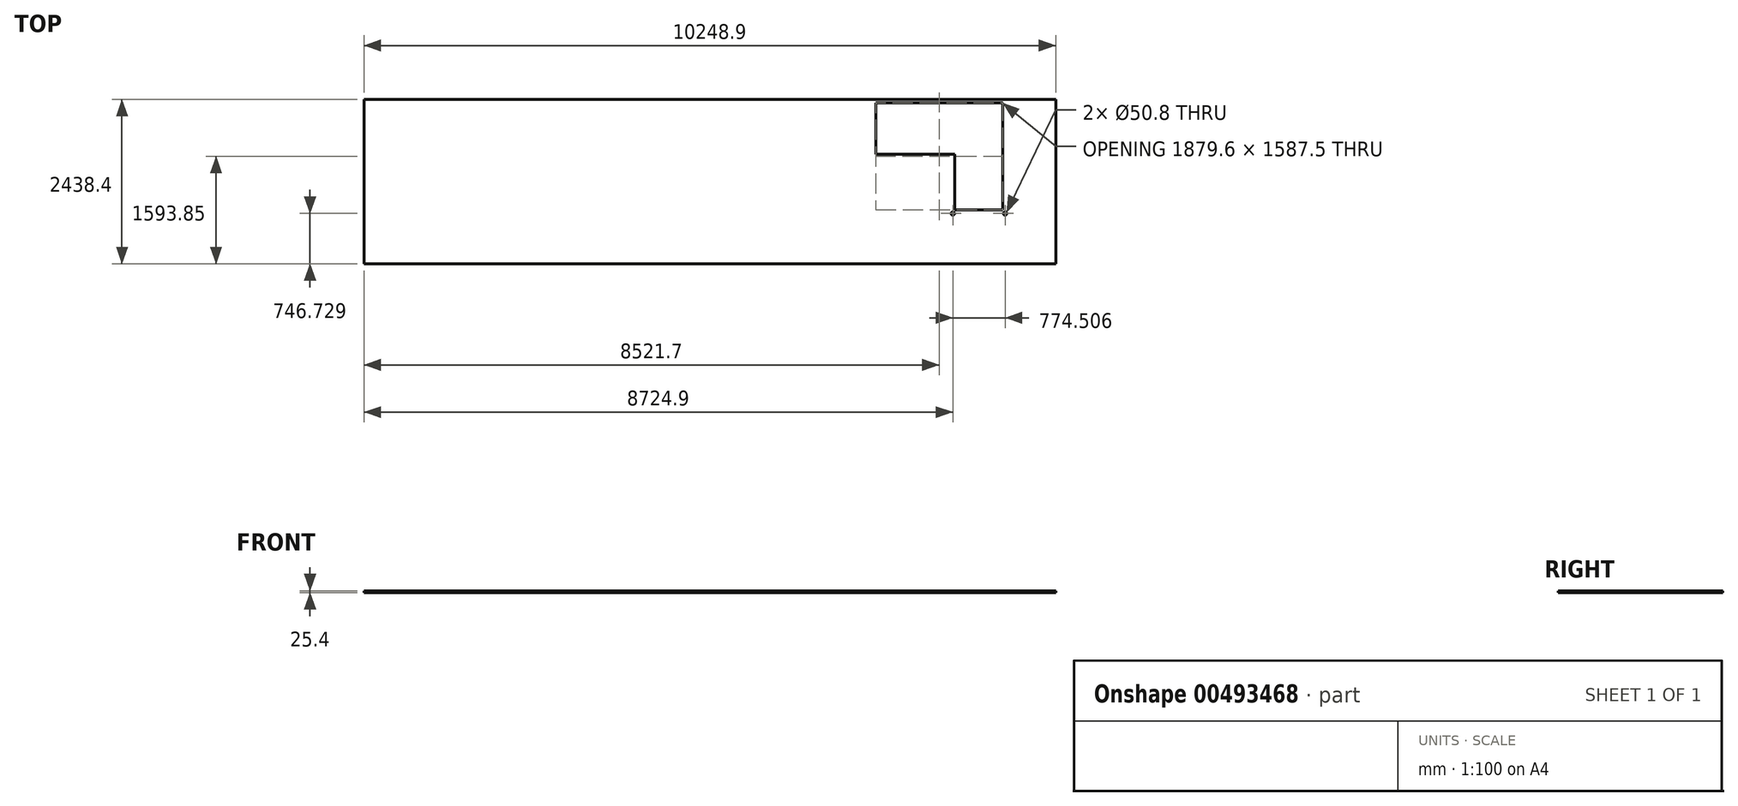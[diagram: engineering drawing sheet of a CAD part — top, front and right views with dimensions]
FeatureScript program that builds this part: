
annotation { "Feature Type Name" : "Feature", "Feature Type Description" : "" }
export const myFeature = defineFeature(function(context is Context, id is Id, definition is map)
    precondition{}
    {
        {
            var Q0;
            Q0=qCreatedBy(makeId("Top.planeOp"),FACE);
            var sketch = newSketch(context, id + "F0", { "sketchPlane" : qUnion([Q0])});
            skLineSegment(sketch, "E0.bottom", {"start": v(-5124.45, 1219.2) * mm, "end": v(5124.45, 1219.2) * mm});
            skLineSegment(sketch, "E0.top", {"start": v(-5124.45, -1219.2) * mm, "end": v(5124.45, -1219.2) * mm});
            skLineSegment(sketch, "E0.left", {"start": v(-5124.45, 1219.2) * mm, "end": v(-5124.45, -1219.2) * mm});
            skLineSegment(sketch, "E0.right", {"start": v(5124.45, 1219.2) * mm, "end": v(5124.45, -1219.2) * mm});
            skPoint(sketch, "E0.middle", {"position": v(0, 0) * mm});
            skLineSegment(sketch, "E1.bottom", {"start": v(-5060.95, 1155.7) * mm, "end": v(-4756.15, 1155.7) * mm});
            skLineSegment(sketch, "E1.top", {"start": v(-5060.95, 850.9) * mm, "end": v(-4756.15, 850.9) * mm});
            skLineSegment(sketch, "E1.left", {"start": v(-5060.95, 1155.7) * mm, "end": v(-5060.95, 850.9) * mm});
            skLineSegment(sketch, "E1.right", {"start": v(-4756.15, 1155.7) * mm, "end": v(-4756.15, 850.9) * mm});
            skLineSegment(sketch, "E2.bottom", {"start": v(-5060.95, -1155.7) * mm, "end": v(-4756.15, -1155.7) * mm});
            skLineSegment(sketch, "E2.top", {"start": v(-5060.95, -850.9) * mm, "end": v(-4756.15, -850.9) * mm});
            skLineSegment(sketch, "E2.left", {"start": v(-5060.95, -1155.7) * mm, "end": v(-5060.95, -850.9) * mm});
            skLineSegment(sketch, "E2.right", {"start": v(-4756.15, -1155.7) * mm, "end": v(-4756.15, -850.9) * mm});
            skLineSegment(sketch, "E3.bottom", {"start": v(1314.45, 1155.7) * mm, "end": v(1619.25, 1155.7) * mm});
            skLineSegment(sketch, "E3.top", {"start": v(1314.45, 850.9) * mm, "end": v(1619.25, 850.9) * mm});
            skLineSegment(sketch, "E3.left", {"start": v(1314.45, 1155.7) * mm, "end": v(1314.45, 850.9) * mm});
            skLineSegment(sketch, "E3.right", {"start": v(1619.25, 1155.7) * mm, "end": v(1619.25, 850.9) * mm});
            skLineSegment(sketch, "E4.bottom", {"start": v(1314.45, -850.9) * mm, "end": v(1619.25, -850.9) * mm});
            skLineSegment(sketch, "E4.top", {"start": v(1314.45, -1155.7) * mm, "end": v(1619.25, -1155.7) * mm});
            skLineSegment(sketch, "E4.left", {"start": v(1314.45, -850.9) * mm, "end": v(1314.45, -1155.7) * mm});
            skLineSegment(sketch, "E4.right", {"start": v(1619.25, -850.9) * mm, "end": v(1619.25, -1155.7) * mm});
            skLineSegment(sketch, "E5", {"start": v(-5124.45, 1155.7) * mm, "end": v(1079.92, 1155.7) * mm, "construction": true});
            skLineSegment(sketch, "E6", {"start": v(-5060.95, -1219.2) * mm, "end": v(-5060.95, 1219.2) * mm, "construction": true});
            skLineSegment(sketch, "E7", {"start": v(-5124.45, -1155.7) * mm, "end": v(1631.36, -1155.7) * mm, "construction": true});
            skLineSegment(sketch, "E8", {"start": v(4337.05, 1168.4) * mm, "end": v(4337.05, -419.1) * mm});
            skLineSegment(sketch, "E9", {"start": v(4337.05, -419.1) * mm, "end": v(3625.85, -419.1) * mm});
            skLineSegment(sketch, "E10", {"start": v(3625.85, -419.1) * mm, "end": v(3625.85, 406.4) * mm});
            skLineSegment(sketch, "E11", {"start": v(3625.85, 406.4) * mm, "end": v(2457.45, 406.4) * mm});
            skLineSegment(sketch, "E12", {"start": v(2457.45, 406.4) * mm, "end": v(2457.45, 1168.4) * mm});
            skLineSegment(sketch, "E13", {"start": v(2457.45, 1168.4) * mm, "end": v(4337.05, 1168.4) * mm});
            skLineSegment(sketch, "E14", {"start": v(5145.06, 1385.01) * mm, "end": v(5145.06, -1378.8) * mm, "construction": true});
            skLineSegment(sketch, "E15", {"start": v(5249.42, -1234.04) * mm, "end": v(3027.6, -1234.04) * mm, "construction": true});
            skLineSegment(sketch, "E16", {"start": v(2212.23, 1274.69) * mm, "end": v(5336.25, 1274.69) * mm, "construction": true});
            skLineSegment(sketch, "E17", {"start": v(3563.42, -472.47) * mm, "end": v(4549.77, -472.47) * mm, "construction": true});
            skLineSegment(sketch, "E18", {"start": v(3600.45, 527.35) * mm, "end": v(3600.45, -613.86) * mm, "construction": true});
            skLineSegment(sketch, "E19", {"start": v(2370.45, 328.73) * mm, "end": v(3770.87, 328.73) * mm, "construction": true});
            skLineSegment(sketch, "E20", {"start": v(2397.38, 1358.85) * mm, "end": v(2397.38, 187.34) * mm, "construction": true});
            skLineSegment(sketch, "E21", {"start": v(4374.96, 1359.95) * mm, "end": v(4374.96, -545.44) * mm, "construction": true});
            skCircle(sketch, "E22", {"center": v(3600.45, -472.47) * mm, "radius": 25.4 * mm});
            skCircle(sketch, "E23", {"center": v(4374.96, -472.47) * mm, "radius": 25.4 * mm});
            skCircle(sketch, "E24", {"center": v(5145.06, -1234.04) * mm, "radius": 25.4 * mm});
            skCircle(sketch, "E25", {"center": v(5145.06, 1274.69) * mm, "radius": 25.4 * mm});
            skCircle(sketch, "E26", {"center": v(2397.38, 1274.69) * mm, "radius": 25.4 * mm});
            skCircle(sketch, "E27", {"center": v(2397.38, 328.73) * mm, "radius": 25.4 * mm});
            skCircle(sketch, "E28", {"center": v(3600.45, 328.73) * mm, "radius": 25.4 * mm});
            skLineSegment(sketch, "E29", {"start": v(2212.23, 1274.69) * mm, "end": v(1295.27, 1274.69) * mm, "construction": true});
            skLineSegment(sketch, "E30", {"start": v(3027.6, -1234.04) * mm, "end": v(1558.73, -1234.04) * mm, "construction": true});
            skPoint(sketch, "E31.orphan", {"position": v(2457.45, 1219.2) * mm});
            skPoint(sketch, "E32.orphan", {"position": v(4337.05, 1219.2) * mm});
            skPoint(sketch, "E33", {"position": v(-4756.15, -1219.2) * mm});
            skPoint(sketch, "E34", {"position": v(-4756.15, 1219.2) * mm});
            skSolve(sketch);
        }
        {
            var Q0;
            Q0=makeQuery(id+"F0.imprint","IMPRINT",FACE,{"disambiguationData":[TD([[makeQuery(id+"F0.imprint","IMPRINT",EDGE,{"derivedFrom":sQuery(id+"F0.wireOp",EDGE,"E0.bottom")}),-1.0]])]});
            var Q1;
            Q1=makeQuery(id+"F0.imprint","IMPRINT",FACE,{"disambiguationData":[TD([[makeQuery(id+"F0.imprint","IMPRINT",EDGE,{"derivedFrom":sQuery(id+"F0.wireOp",EDGE,"07bb9709-c2e3-4458-9c75-e7e0cda7abd20.MirrorCS")}),1.0]])]});
            var Q2;
            Q2=makeQuery(id+"F0.imprint","IMPRINT",FACE,{"disambiguationData":[TD([[makeQuery(id+"F0.imprint","IMPRINT",EDGE,{"derivedFrom":sQuery(id+"F0.wireOp",EDGE,"84134bc9-2361-4c5e-a1d2-2466ce79142d0.MirrorCS")}),1.0]])]});
            var Q3;
            Q3=makeQuery(id+"F0.imprint","IMPRINT",FACE,{"disambiguationData":[TD([[makeQuery(id+"F0.imprint","IMPRINT",EDGE,{"derivedFrom":sQuery(id+"F0.wireOp",EDGE,"b2089bdf-4319-4673-ba67-9373ea4a7545.1.0.0")}),1.0]])]});
            var Q4;
            Q4=makeQuery(id+"F0.imprint","IMPRINT",FACE,{"disambiguationData":[TD([[makeQuery(id+"F0.imprint","IMPRINT",EDGE,{"derivedFrom":sQuery(id+"F0.wireOp",EDGE,"b2089bdf-4319-4673-ba67-9373ea4a7545.1.0.4")}),1.0]])]});
            var Q5;
            Q5=makeQuery(id+"F0.imprint","IMPRINT",FACE,{"disambiguationData":[TD([[makeQuery(id+"F0.imprint","IMPRINT",EDGE,{"derivedFrom":sQuery(id+"F0.wireOp",EDGE,"E1.bottom")}),-1.0]])]});
            var Q6;
            Q6=makeQuery(id+"F0.imprint","IMPRINT",FACE,{"disambiguationData":[TD([[makeQuery(id+"F0.imprint","IMPRINT",EDGE,{"derivedFrom":sQuery(id+"F0.wireOp",EDGE,"E3.bottom")}),-1.0]])]});
            var Q7;
            Q7=makeQuery(id+"F0.imprint","IMPRINT",FACE,{"disambiguationData":[TD([[makeQuery(id+"F0.imprint","IMPRINT",EDGE,{"derivedFrom":sQuery(id+"F0.wireOp",EDGE,"E4.bottom")}),-1.0]])]});
            var Q8;
            Q8=makeQuery(id+"F0.imprint","IMPRINT",FACE,{"disambiguationData":[TD([[makeQuery(id+"F0.imprint","IMPRINT",EDGE,{"derivedFrom":sQuery(id+"F0.wireOp",EDGE,"E2.bottom")}),1.0]])]});
            var Q9;
            {var subQ5=sQuery(id+"F0.wireOp",EDGE,"E13");Q9=makeQuery(id+"F0.imprint","IMPRINT",FACE,{"disambiguationData":[TD([[makeQuery(id+"F0.imprint","IMPRINT",EDGE,{"derivedFrom":subQ5}),1.0]])]});}
            var Q10;
            Q10=makeQuery(id+"F0.imprint","IMPRINT",FACE,{"disambiguationData":[TD([[makeQuery(id+"F0.imprint","IMPRINT",EDGE,{"derivedFrom":sQuery(id+"F0.wireOp",EDGE,"E28")}),1.0]])]});
            var Q11;
            Q11=makeQuery(id+"F0.imprint","IMPRINT",FACE,{"disambiguationData":[TD([[makeQuery(id+"F0.imprint","IMPRINT",EDGE,{"derivedFrom":sQuery(id+"F0.wireOp",EDGE,"E27")}),1.0]])]});
            extrude(context, id + "F1", {"entities" : qUnion([Q0, Q1, Q2, Q3, Q4, Q5, Q6, Q7, Q8, Q9, Q10, Q11]), "depth" : 25.4 * mm, "offsetDistance" : 25.4 * mm});
        }
        {
            var Q0;
            Q0=makeQuery(id+"F1.opExtrude","CAP_FACE",FACE,{"disambiguationData":[OSD([sQuery(id+"F0.wireOp",EDGE,"E0.bottom"),sQuery(id+"F0.wireOp",EDGE,"E0.top"),sQuery(id+"F0.wireOp",EDGE,"E0.left"),sQuery(id+"F0.wireOp",EDGE,"E0.right"),sQuery(id+"F0.wireOp",EDGE,"E8"),sQuery(id+"F0.wireOp",EDGE,"E9"),sQuery(id+"F0.wireOp",EDGE,"E10"),sQuery(id+"F0.wireOp",EDGE,"E11"),sQuery(id+"F0.wireOp",EDGE,"E12")])],"isStart":false});
            var sketch = newSketch(context, id + "F2", { "sketchPlane" : qUnion([Q0])});
            skLineSegment(sketch, "E35.0", {"start": v(-4756.15, 1155.7) * mm, "end": v(-4756.15, 850.9) * mm});
            skLineSegment(sketch, "E35.1", {"start": v(-5124.45, 1155.7) * mm, "end": v(1079.92, 1155.7) * mm});
            skLineSegment(sketch, "E35.2", {"start": v(-5060.95, 850.9) * mm, "end": v(-4756.15, 850.9) * mm});
            skLineSegment(sketch, "E35.3", {"start": v(-5060.95, 1155.7) * mm, "end": v(-4756.15, 1155.7) * mm});
            skLineSegment(sketch, "E35.4", {"start": v(-5060.95, 1155.7) * mm, "end": v(-5060.95, 850.9) * mm});
            skLineSegment(sketch, "E35.5", {"start": v(-5060.95, -1219.2) * mm, "end": v(-5060.95, 1219.2) * mm});
            skLineSegment(sketch, "E36.0", {"start": v(-5124.45, -1155.7) * mm, "end": v(1631.36, -1155.7) * mm});
            skLineSegment(sketch, "E36.1", {"start": v(-5060.95, -850.9) * mm, "end": v(-4756.15, -850.9) * mm});
            skLineSegment(sketch, "E36.2", {"start": v(-5060.95, -1155.7) * mm, "end": v(-4756.15, -1155.7) * mm});
            skLineSegment(sketch, "E36.3", {"start": v(-4756.15, -1155.7) * mm, "end": v(-4756.15, -850.9) * mm});
            skLineSegment(sketch, "E36.4", {"start": v(-5060.95, -1155.7) * mm, "end": v(-5060.95, -850.9) * mm});
            skLineSegment(sketch, "E37.0", {"start": v(1619.25, -850.9) * mm, "end": v(1619.25, -1155.7) * mm});
            skLineSegment(sketch, "E37.1", {"start": v(1314.45, -850.9) * mm, "end": v(1619.25, -850.9) * mm});
            skLineSegment(sketch, "E37.2", {"start": v(1314.45, -850.9) * mm, "end": v(1314.45, -1155.7) * mm});
            skLineSegment(sketch, "E37.3", {"start": v(1314.45, -1155.7) * mm, "end": v(1619.25, -1155.7) * mm});
            skLineSegment(sketch, "E38.0", {"start": v(1619.25, 1155.7) * mm, "end": v(1619.25, 850.9) * mm});
            skLineSegment(sketch, "E38.1", {"start": v(1314.45, 1155.7) * mm, "end": v(1619.25, 1155.7) * mm});
            skLineSegment(sketch, "E38.2", {"start": v(1314.45, 850.9) * mm, "end": v(1619.25, 850.9) * mm});
            skLineSegment(sketch, "E38.3", {"start": v(-5124.45, 1219.2) * mm, "end": v(5124.45, 1219.2) * mm});
            skLineSegment(sketch, "E38.4", {"start": v(1314.45, 1155.7) * mm, "end": v(1314.45, 850.9) * mm});
            skSolve(sketch);
        }
    });
